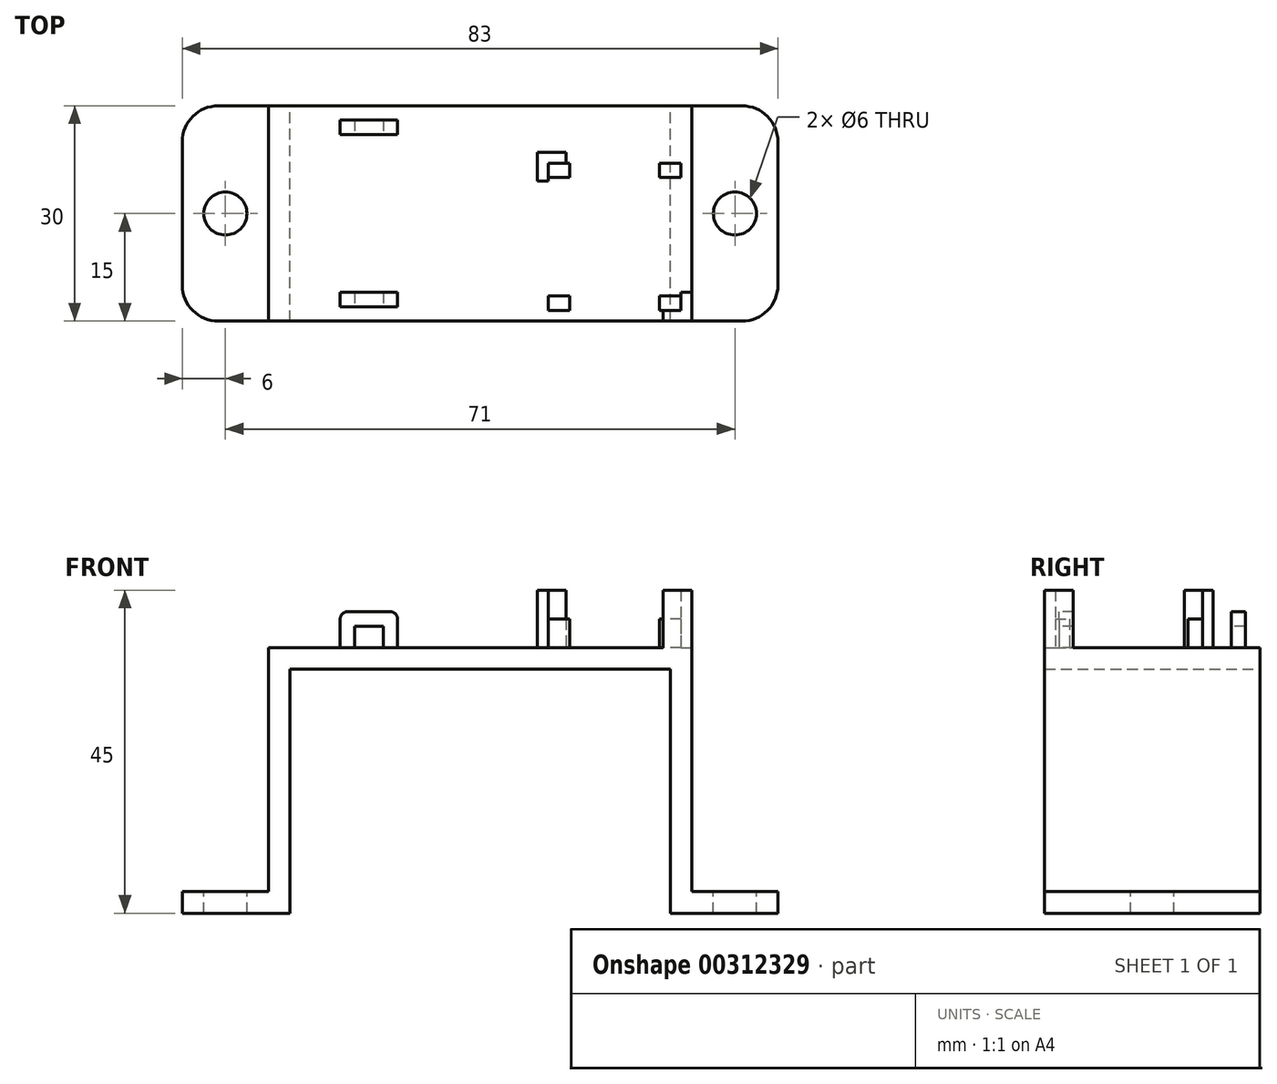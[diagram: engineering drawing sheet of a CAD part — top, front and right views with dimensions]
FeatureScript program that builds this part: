
annotation { "Feature Type Name" : "Feature", "Feature Type Description" : "" }
export const myFeature = defineFeature(function(context is Context, id is Id, definition is map)
    precondition{}
    {
        {
            var Q0;
            Q0=qCreatedBy(makeId("Front.planeOp"),FACE);
            var sketch = newSketch(context, id + "F0", { "sketchPlane" : qUnion([Q0])});
            skLineSegment(sketch, "E0", {"start": v(0, 0) * mm, "end": v(15, 0) * mm});
            skLineSegment(sketch, "E1", {"start": v(15, 0) * mm, "end": v(15, 34) * mm});
            skLineSegment(sketch, "E2", {"start": v(15, 34) * mm, "end": v(68, 34) * mm});
            skLineSegment(sketch, "E3", {"start": v(68, 34) * mm, "end": v(68, 0) * mm});
            skLineSegment(sketch, "E4", {"start": v(68, 0) * mm, "end": v(83, 0) * mm});
            skLineSegment(sketch, "E5.0", {"start": v(71, 3) * mm, "end": v(83, 3) * mm});
            skLineSegment(sketch, "E5.1", {"start": v(0, 3) * mm, "end": v(12, 3) * mm});
            skLineSegment(sketch, "E5.2", {"start": v(12, 3) * mm, "end": v(12, 37) * mm});
            skLineSegment(sketch, "E5.3", {"start": v(12, 37) * mm, "end": v(71, 37) * mm});
            skLineSegment(sketch, "E5.4", {"start": v(71, 37) * mm, "end": v(71, 3) * mm});
            skLineSegment(sketch, "E6", {"start": v(0, 3) * mm, "end": v(0, 0) * mm});
            skLineSegment(sketch, "E7", {"start": v(83, 3) * mm, "end": v(83, 0) * mm});
            skSolve(sketch);
        }
        {
            var Q0;
            Q0 = qSketchRegion(id + "F0", true);
            extrude(context, id + "F1", {"entities" : qUnion([Q0]), "depth" : 30 * mm});
        }
        {
            var Q0;
            Q0=makeQuery(id+"F1.opExtrude","SWEPT_FACE",FACE,{"disambiguationData":[OSD([sQuery(id+"F0.wireOp",EDGE,"E5.1")])]});
            var sketch = newSketch(context, id + "F2", { "sketchPlane" : qUnion([Q0])});
            skCircle(sketch, "E8", {"center": v(6, -15) * mm, "radius": 3 * mm});
            skCircle(sketch, "E9", {"center": v(77, -15) * mm, "radius": 3 * mm});
            skSolve(sketch);
        }
        {
            var Q0;
            Q0 = qSketchRegion(id + "F2", true);
            extrude(context, id + "F3", {"entities" : qUnion([Q0]), "operationType" : NewBodyOperationType.REMOVE, "endBound" : BoundingType.THROUGH_ALL, "oppositeDirection" : true, "depth" : 25 * mm});
        }
        {
            var Q0;
            Q0=makeQuery(id+"F1.opExtrude","SWEPT_FACE",FACE,{"disambiguationData":[OSD([sQuery(id+"F0.wireOp",EDGE,"E5.3")])]});
            var sketch = newSketch(context, id + "F4", { "sketchPlane" : qUnion([Q0])});
            skLineSegment(sketch, "E10", {"start": v(71, -26) * mm, "end": v(71, -30) * mm});
            skLineSegment(sketch, "E11", {"start": v(71, -30) * mm, "end": v(67, -30) * mm});
            skLineSegment(sketch, "E12", {"start": v(67, -30) * mm, "end": v(67, -28.5) * mm});
            skLineSegment(sketch, "E13", {"start": v(67, -28.5) * mm, "end": v(69.5, -28.5) * mm});
            skLineSegment(sketch, "E14", {"start": v(69.5, -28.5) * mm, "end": v(69.5, -26) * mm});
            skLineSegment(sketch, "E15", {"start": v(69.5, -26) * mm, "end": v(71, -26) * mm});
            skLineSegment(sketch, "E16", {"start": v(49.5, -6.5) * mm, "end": v(49.5, -10.5) * mm});
            skLineSegment(sketch, "E17", {"start": v(49.5, -10.5) * mm, "end": v(51, -10.5) * mm});
            skLineSegment(sketch, "E18", {"start": v(51, -10.5) * mm, "end": v(51, -8) * mm});
            skLineSegment(sketch, "E19", {"start": v(51, -8) * mm, "end": v(53.5, -8) * mm});
            skLineSegment(sketch, "E20", {"start": v(53.5, -6.5) * mm, "end": v(53.5, -8) * mm});
            skLineSegment(sketch, "E21", {"start": v(53.5, -6.5) * mm, "end": v(49.5, -6.5) * mm});
            skSolve(sketch);
        }
        {
            var Q0;
            Q0 = qSketchRegion(id + "F4", true);
            extrude(context, id + "F5", {"entities" : qUnion([Q0]), "operationType" : NewBodyOperationType.ADD, "depth" : 8 * mm});
        }
        {
            var Q0;
            Q0=makeQuery(id+"F1.opExtrude","SWEPT_FACE",FACE,{"disambiguationData":[OSD([sQuery(id+"F0.wireOp",EDGE,"E5.3")])]});
            var sketch = newSketch(context, id + "F6", { "sketchPlane" : qUnion([Q0])});
            skLineSegment(sketch, "E22.bottom", {"start": v(22, -2) * mm, "end": v(30, -2) * mm});
            skLineSegment(sketch, "E22.top", {"start": v(22, -4) * mm, "end": v(30, -4) * mm});
            skLineSegment(sketch, "E22.left", {"start": v(22, -2) * mm, "end": v(22, -4) * mm});
            skLineSegment(sketch, "E22.right", {"start": v(30, -2) * mm, "end": v(30, -4) * mm});
            skLineSegment(sketch, "E23.bottom", {"start": v(22, -26) * mm, "end": v(30, -26) * mm});
            skLineSegment(sketch, "E23.top", {"start": v(22, -28) * mm, "end": v(30, -28) * mm});
            skLineSegment(sketch, "E23.left", {"start": v(22, -26) * mm, "end": v(22, -28) * mm});
            skLineSegment(sketch, "E23.right", {"start": v(30, -26) * mm, "end": v(30, -28) * mm});
            skSolve(sketch);
        }
        {
            var Q0;
            Q0 = qSketchRegion(id + "F6", true);
            extrude(context, id + "F7", {"entities" : qUnion([Q0]), "operationType" : NewBodyOperationType.ADD, "depth" : 5 * mm});
        }
        {
            var Q0;
            Q0=makeQuery(id+"F1.opExtrude","SWEPT_FACE",FACE,{"disambiguationData":[OSD([sQuery(id+"F0.wireOp",EDGE,"E5.3")])]});
            var sketch = newSketch(context, id + "F8", { "sketchPlane" : qUnion([Q0])});
            skLineSegment(sketch, "E24.bottom", {"start": v(51, -8) * mm, "end": v(54, -8) * mm});
            skLineSegment(sketch, "E24.top", {"start": v(51, -10) * mm, "end": v(54, -10) * mm});
            skLineSegment(sketch, "E24.left", {"start": v(51, -8) * mm, "end": v(51, -10) * mm});
            skLineSegment(sketch, "E24.right", {"start": v(54, -8) * mm, "end": v(54, -10) * mm});
            skLineSegment(sketch, "E25.bottom", {"start": v(69.5, -28.5) * mm, "end": v(66.5, -28.5) * mm});
            skLineSegment(sketch, "E25.top", {"start": v(69.5, -26.5) * mm, "end": v(66.5, -26.5) * mm});
            skLineSegment(sketch, "E25.left", {"start": v(69.5, -28.5) * mm, "end": v(69.5, -26.5) * mm});
            skLineSegment(sketch, "E25.right", {"start": v(66.5, -28.5) * mm, "end": v(66.5, -26.5) * mm});
            skLineSegment(sketch, "E26.bottom", {"start": v(66.5, -8) * mm, "end": v(69.5, -8) * mm});
            skLineSegment(sketch, "E26.top", {"start": v(66.5, -10) * mm, "end": v(69.5, -10) * mm});
            skLineSegment(sketch, "E26.left", {"start": v(66.5, -8) * mm, "end": v(66.5, -10) * mm});
            skLineSegment(sketch, "E26.right", {"start": v(69.5, -8) * mm, "end": v(69.5, -10) * mm});
            skLineSegment(sketch, "E27.bottom", {"start": v(51, -26.5) * mm, "end": v(54, -26.5) * mm});
            skLineSegment(sketch, "E27.top", {"start": v(51, -28.5) * mm, "end": v(54, -28.5) * mm});
            skLineSegment(sketch, "E27.left", {"start": v(51, -26.5) * mm, "end": v(51, -28.5) * mm});
            skLineSegment(sketch, "E27.right", {"start": v(54, -26.5) * mm, "end": v(54, -28.5) * mm});
            skSolve(sketch);
        }
        {
            var Q0;
            Q0 = qSketchRegion(id + "F8", true);
            extrude(context, id + "F9", {"entities" : qUnion([Q0]), "operationType" : NewBodyOperationType.ADD, "depth" : 4 * mm});
        }
        {
            var Q0;
            Q0=makeQuery(id+"F7.opExtrude","SWEPT_FACE",FACE,{"disambiguationData":[OSD([sQuery(id+"F6.wireOp",EDGE,"E23.top")])]});
            var sketch = newSketch(context, id + "F10", { "sketchPlane" : qUnion([Q0])});
            skLineSegment(sketch, "E28.bottom", {"start": v(24, 40) * mm, "end": v(28, 40) * mm});
            skLineSegment(sketch, "E28.top", {"start": v(24, 37) * mm, "end": v(28, 37) * mm});
            skLineSegment(sketch, "E28.left", {"start": v(24, 40) * mm, "end": v(24, 37) * mm});
            skLineSegment(sketch, "E28.right", {"start": v(28, 40) * mm, "end": v(28, 37) * mm});
            skSolve(sketch);
        }
        {
            var Q0;
            Q0 = qSketchRegion(id + "F10", true);
            extrude(context, id + "F11", {"entities" : qUnion([Q0]), "operationType" : NewBodyOperationType.REMOVE, "endBound" : BoundingType.THROUGH_ALL, "oppositeDirection" : true, "depth" : 25 * mm});
        }
        {
            var Q0;
            Q0=makeQuery(id+"F7.opExtrude","CAP_EDGE",EDGE,{"disambiguationData":[OSD([sQuery(id+"F6.wireOp",EDGE,"E23.right")])],"isStart":false});
            var Q1;
            Q1=makeQuery(id+"F7.opExtrude","CAP_EDGE",EDGE,{"disambiguationData":[OSD([sQuery(id+"F6.wireOp",EDGE,"E22.right")])],"isStart":false});
            var Q2;
            Q2=makeQuery(id+"F7.opExtrude","CAP_EDGE",EDGE,{"disambiguationData":[OSD([sQuery(id+"F6.wireOp",EDGE,"E22.left")])],"isStart":false});
            var Q3;
            Q3=makeQuery(id+"F7.opExtrude","CAP_EDGE",EDGE,{"disambiguationData":[OSD([sQuery(id+"F6.wireOp",EDGE,"E23.left")])],"isStart":false});
            var Q4;
            Q4=makeQuery(id+"F7.opExtrude","CAP_EDGE",EDGE,{"disambiguationData":[OSD([sQuery(id+"F6.wireOp",EDGE,"E23.left")])],"isStart":true});
            var Q5;
            Q5=makeQuery(id+"F7.opExtrude","CAP_EDGE",EDGE,{"disambiguationData":[OSD([sQuery(id+"F6.wireOp",EDGE,"E22.left")])],"isStart":true});
            var Q6;
            {var subQ0=sQuery(id+"F6.wireOp",EDGE,"E22.top");Q6=makeQuery(id+"F11.boolean.opBoolean","SPLIT",EDGE,{"disambiguationData":[TD([makeQuery(id+"F7.opExtrude","SWEPT_FACE",FACE,{"disambiguationData":[OSD([sQuery(id+"F6.wireOp",EDGE,"E22.left")])]})])],"derivedFrom":makeQuery(id+"F7.opExtrude","CAP_EDGE",EDGE,{"disambiguationData":[OSD([subQ0])],"isStart":true})});}
            var Q7;
            Q7=makeQuery(id+"F7.opExtrude","CAP_EDGE",EDGE,{"disambiguationData":[OSD([sQuery(id+"F6.wireOp",EDGE,"E22.right")])],"isStart":true});
            var Q8;
            {var subQ0=sQuery(id+"F6.wireOp",EDGE,"E22.top");Q8=makeQuery(id+"F11.boolean.opBoolean","SPLIT",EDGE,{"disambiguationData":[TD([makeQuery(id+"F7.opExtrude","SWEPT_FACE",FACE,{"disambiguationData":[OSD([sQuery(id+"F6.wireOp",EDGE,"E22.right")])]})])],"derivedFrom":makeQuery(id+"F7.opExtrude","CAP_EDGE",EDGE,{"disambiguationData":[OSD([subQ0])],"isStart":true})});}
            var Q9;
            {var subQ0=sQuery(id+"F6.wireOp",EDGE,"E23.top");Q9=makeQuery(id+"F11.boolean.opBoolean","SPLIT",EDGE,{"disambiguationData":[TD([makeQuery(id+"F7.opExtrude","SWEPT_FACE",FACE,{"disambiguationData":[OSD([sQuery(id+"F6.wireOp",EDGE,"E23.left")])]})])],"derivedFrom":makeQuery(id+"F7.opExtrude","CAP_EDGE",EDGE,{"disambiguationData":[OSD([subQ0])],"isStart":true})});}
            var Q10;
            {var subQ0=sQuery(id+"F6.wireOp",EDGE,"E23.top");Q10=makeQuery(id+"F11.boolean.opBoolean","SPLIT",EDGE,{"disambiguationData":[TD([makeQuery(id+"F7.opExtrude","SWEPT_FACE",FACE,{"disambiguationData":[OSD([sQuery(id+"F6.wireOp",EDGE,"E23.right")])]})])],"derivedFrom":makeQuery(id+"F7.opExtrude","CAP_EDGE",EDGE,{"disambiguationData":[OSD([subQ0])],"isStart":true})});}
            var Q11;
            Q11=makeQuery(id+"F7.opExtrude","CAP_EDGE",EDGE,{"disambiguationData":[OSD([sQuery(id+"F6.wireOp",EDGE,"E23.right")])],"isStart":true});
            var Q12;
            {var subQ0=sQuery(id+"F6.wireOp",EDGE,"E23.bottom");Q12=makeQuery(id+"F11.boolean.opBoolean","SPLIT",EDGE,{"disambiguationData":[TD([makeQuery(id+"F7.opExtrude","SWEPT_FACE",FACE,{"disambiguationData":[OSD([sQuery(id+"F6.wireOp",EDGE,"E23.left")])]})])],"derivedFrom":makeQuery(id+"F7.opExtrude","CAP_EDGE",EDGE,{"disambiguationData":[OSD([subQ0])],"isStart":true})});}
            var Q13;
            {var subQ0=sQuery(id+"F6.wireOp",EDGE,"E23.bottom");Q13=makeQuery(id+"F11.boolean.opBoolean","SPLIT",EDGE,{"disambiguationData":[TD([makeQuery(id+"F7.opExtrude","SWEPT_FACE",FACE,{"disambiguationData":[OSD([sQuery(id+"F6.wireOp",EDGE,"E23.right")])]})])],"derivedFrom":makeQuery(id+"F7.opExtrude","CAP_EDGE",EDGE,{"disambiguationData":[OSD([subQ0])],"isStart":true})});}
            var Q14;
            {var subQ0=sQuery(id+"F6.wireOp",EDGE,"E22.bottom");Q14=makeQuery(id+"F11.boolean.opBoolean","SPLIT",EDGE,{"disambiguationData":[TD([makeQuery(id+"F7.opExtrude","SWEPT_FACE",FACE,{"disambiguationData":[OSD([sQuery(id+"F6.wireOp",EDGE,"E22.right")])]})])],"derivedFrom":makeQuery(id+"F7.opExtrude","CAP_EDGE",EDGE,{"disambiguationData":[OSD([subQ0])],"isStart":true})});}
            var Q15;
            {var subQ0=sQuery(id+"F6.wireOp",EDGE,"E22.bottom");Q15=makeQuery(id+"F11.boolean.opBoolean","SPLIT",EDGE,{"disambiguationData":[TD([makeQuery(id+"F7.opExtrude","SWEPT_FACE",FACE,{"disambiguationData":[OSD([sQuery(id+"F6.wireOp",EDGE,"E22.left")])]})])],"derivedFrom":makeQuery(id+"F7.opExtrude","CAP_EDGE",EDGE,{"disambiguationData":[OSD([subQ0])],"isStart":true})});}
            var Q16;
            Q16=makeQuery(id+"F5.opExtrude","CAP_EDGE",EDGE,{"disambiguationData":[OSD([sQuery(id+"F4.wireOp",EDGE,"E21")])],"isStart":true});
            var Q17;
            Q17=makeQuery(id+"F5.opExtrude","CAP_EDGE",EDGE,{"disambiguationData":[OSD([sQuery(id+"F4.wireOp",EDGE,"E16")])],"isStart":true});
            var Q18;
            Q18=makeQuery(id+"F5.opExtrude","CAP_EDGE",EDGE,{"disambiguationData":[OSD([sQuery(id+"F4.wireOp",EDGE,"E17")])],"isStart":true});
            fillet(context, id + "F12", {"entities" : qUnion([Q0, Q1, Q2, Q3, Q4, Q5, Q6, Q7, Q8, Q9, Q10, Q11, Q12, Q13, Q14, Q15, Q16, Q17, Q18]), "radius" : 1 * mm, "tangentPropagation" : true, "allowEdgeOverflow" : false});
        }
        {
            var Q0;
            Q0=makeQuery(id+"F1.opExtrude","CAP_EDGE",EDGE,{"disambiguationData":[OSD([sQuery(id+"F0.wireOp",EDGE,"E7")])],"isStart":false});
            var Q1;
            Q1=makeQuery(id+"F1.opExtrude","CAP_EDGE",EDGE,{"disambiguationData":[OSD([sQuery(id+"F0.wireOp",EDGE,"E7")])],"isStart":true});
            var Q2;
            Q2=makeQuery(id+"F1.opExtrude","CAP_EDGE",EDGE,{"disambiguationData":[OSD([sQuery(id+"F0.wireOp",EDGE,"E6")])],"isStart":true});
            var Q3;
            Q3=makeQuery(id+"F1.opExtrude","CAP_EDGE",EDGE,{"disambiguationData":[OSD([sQuery(id+"F0.wireOp",EDGE,"E6")])],"isStart":false});
            fillet(context, id + "F13", {"entities" : qUnion([Q0, Q1, Q2, Q3]), "radius" : 5 * mm, "tangentPropagation" : true, "allowEdgeOverflow" : false});
        }
    });
